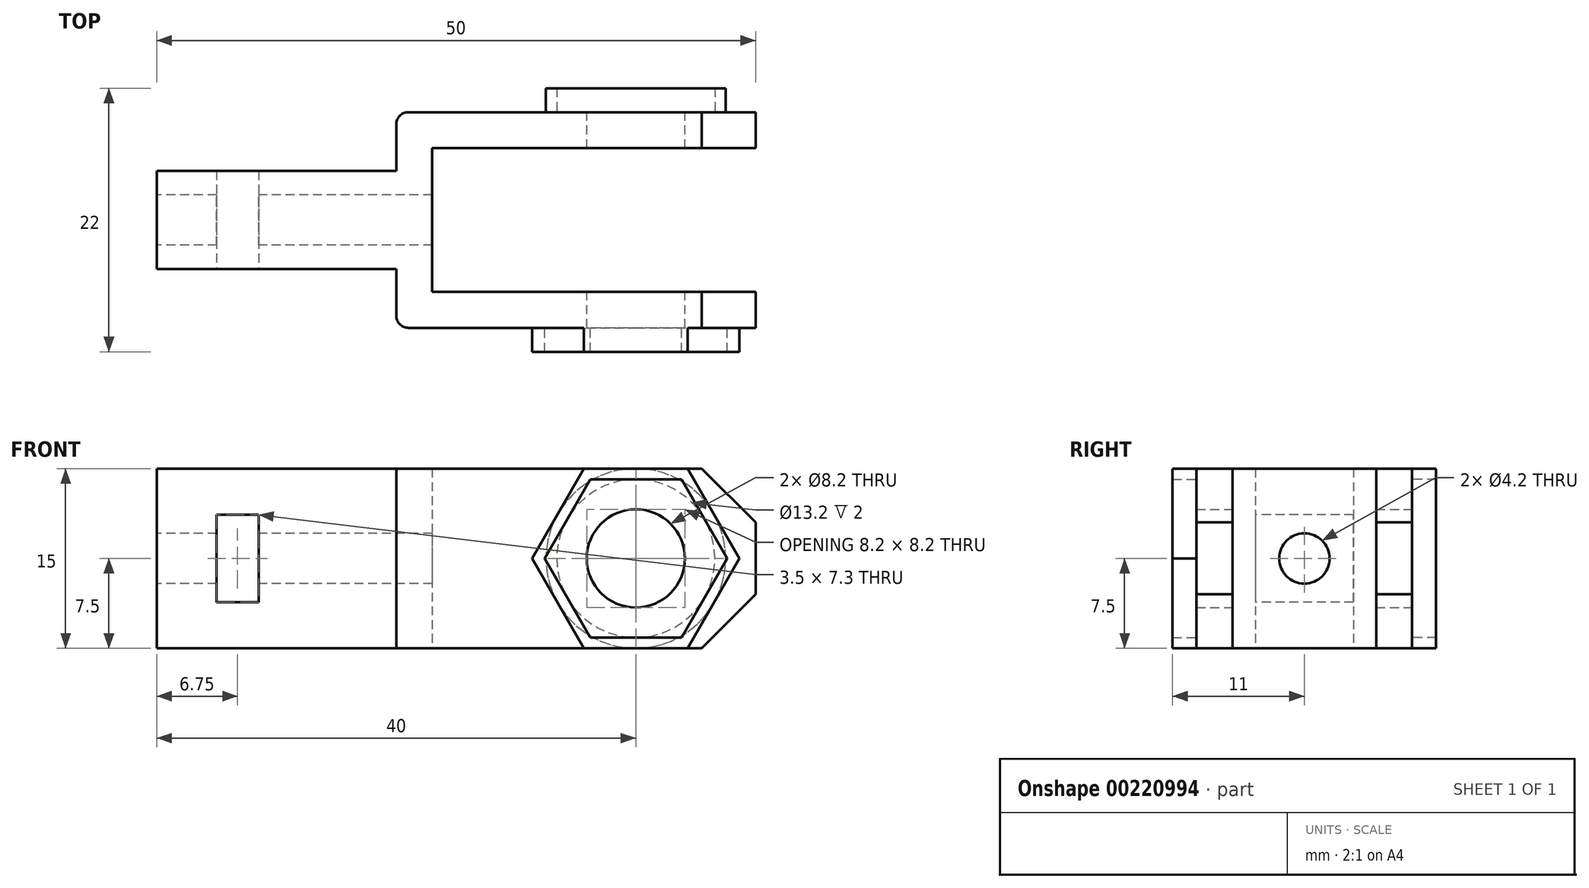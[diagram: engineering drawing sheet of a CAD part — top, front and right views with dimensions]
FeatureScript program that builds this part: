
annotation { "Feature Type Name" : "Feature", "Feature Type Description" : "" }
export const myFeature = defineFeature(function(context is Context, id is Id, definition is map)
    precondition{}
    {
        {
            var Q0;
            Q0=qCreatedBy(makeId("Top.planeOp"),FACE);
            var sketch = newSketch(context, id + "F0", { "sketchPlane" : qUnion([Q0])});
            skLineSegment(sketch, "E0", {"start": v(0, 0) * mm, "end": v(0, 4.1) * mm});
            skLineSegment(sketch, "E1", {"start": v(0, 4.1) * mm, "end": v(20, 4.1) * mm});
            skLineSegment(sketch, "E2", {"start": v(20, 4.1) * mm, "end": v(20, 8) * mm});
            skLineSegment(sketch, "E3", {"start": v(21, 9) * mm, "end": v(50, 9) * mm});
            skLineSegment(sketch, "E4", {"start": v(50, 9) * mm, "end": v(50, 6) * mm});
            skLineSegment(sketch, "E5", {"start": v(50, 6) * mm, "end": v(23, 6) * mm});
            skLineSegment(sketch, "E6", {"start": v(23, 6) * mm, "end": v(23, 0) * mm});
            skLineSegment(sketch, "E7.MirrorCS", {"start": v(50, -9) * mm, "end": v(50, -6) * mm});
            skLineSegment(sketch, "E8.MirrorCS", {"start": v(0, 0) * mm, "end": v(0, -4.1) * mm});
            skLineSegment(sketch, "E9.MirrorCS", {"start": v(23, -6) * mm, "end": v(23, 0) * mm});
            skLineSegment(sketch, "E10.MirrorCS", {"start": v(50, -6) * mm, "end": v(23, -6) * mm});
            skLineSegment(sketch, "E11.MirrorCS", {"start": v(21, -9) * mm, "end": v(50, -9) * mm});
            skLineSegment(sketch, "E12.MirrorCS", {"start": v(0, -4.1) * mm, "end": v(20, -4.1) * mm});
            skLineSegment(sketch, "E13.MirrorCS", {"start": v(20, -4.1) * mm, "end": v(20, -8) * mm});
            skPoint(sketch, "E14.visualSharp", {"position": v(20, 9) * mm});
            skArc(sketch, "E14.filletArc", {"start": v(21, 9) * mm, "mid": v(20.3, 8.7) * mm, "end": v(20, 8) * mm});
            skPoint(sketch, "E15.visualSharp", {"position": v(20, -9) * mm});
            skArc(sketch, "E15.filletArc", {"start": v(20, -8) * mm, "mid": v(20.3, -8.7) * mm, "end": v(21, -9) * mm});
            skSolve(sketch);
        }
        {
            var Q0;
            Q0 = qSketchRegion(id + "F0", true);
            extrude(context, id + "F1", {"entities" : qUnion([Q0]), "depth" : 15 * mm});
        }
        {
            var Q0;
            Q0=makeQuery(id+"F1.opExtrude","SWEPT_FACE",FACE,{"disambiguationData":[OSD([sQuery(id+"F0.wireOp",EDGE,"E0"),sQuery(id+"F0.wireOp",EDGE,"E8.MirrorCS")])]});
            var sketch = newSketch(context, id + "F2", { "sketchPlane" : qUnion([Q0])});
            skLineSegment(sketch, "E16", {"start": v(0, 0) * mm, "end": v(0, 15) * mm, "construction": true});
            skCircle(sketch, "E17", {"center": v(0, 7.5) * mm, "radius": 2.1 * mm});
            skSolve(sketch);
        }
        {
            var Q0;
            Q0 = qSketchRegion(id + "F2", true);
            extrude(context, id + "F3", {"entities" : qUnion([Q0]), "operationType" : NewBodyOperationType.REMOVE, "endBound" : BoundingType.THROUGH_ALL, "oppositeDirection" : true, "depth" : 25 * mm});
        }
        {
            var Q0;
            Q0=makeQuery(id+"F1.opExtrude","SWEPT_FACE",FACE,{"disambiguationData":[OSD([sQuery(id+"F0.wireOp",EDGE,"E12.MirrorCS")])]});
            var sketch = newSketch(context, id + "F4", { "sketchPlane" : qUnion([Q0])});
            skLineSegment(sketch, "E18", {"start": v(0, 7.5) * mm, "end": v(20, 7.5) * mm, "construction": true});
            skLineSegment(sketch, "E19.bottom", {"start": v(5, 11.15) * mm, "end": v(8.5, 11.15) * mm});
            skLineSegment(sketch, "E19.top", {"start": v(5, 3.85) * mm, "end": v(8.5, 3.85) * mm});
            skLineSegment(sketch, "E19.left", {"start": v(5, 11.15) * mm, "end": v(5, 3.85) * mm});
            skLineSegment(sketch, "E19.right", {"start": v(8.5, 11.15) * mm, "end": v(8.5, 3.85) * mm});
            skPoint(sketch, "E19.middle", {"position": v(6.75, 7.5) * mm});
            skSolve(sketch);
        }
        {
            var Q0;
            Q0 = qSketchRegion(id + "F4", true);
            extrude(context, id + "F5", {"entities" : qUnion([Q0]), "operationType" : NewBodyOperationType.REMOVE, "endBound" : BoundingType.THROUGH_ALL, "oppositeDirection" : true, "depth" : 25 * mm});
        }
        {
            var Q0;
            Q0=makeQuery(id+"F1.opExtrude","SWEPT_FACE",FACE,{"disambiguationData":[OSD([sQuery(id+"F0.wireOp",EDGE,"E3")])]});
            var sketch = newSketch(context, id + "F6", { "sketchPlane" : qUnion([Q0])});
            skLineSegment(sketch, "E20", {"start": v(-50, 7.5) * mm, "end": v(-21, 7.5) * mm, "construction": true});
            skCircle(sketch, "E21", {"center": v(-40, 7.5) * mm, "radius": 4.1 * mm});
            skLineSegment(sketch, "E22", {"start": v(-50, 15) * mm, "end": v(-45.5, 15) * mm});
            skLineSegment(sketch, "E23", {"start": v(-45.5, 15) * mm, "end": v(-50, 10.5) * mm});
            skLineSegment(sketch, "E24", {"start": v(-50, 10.5) * mm, "end": v(-50, 15) * mm});
            skLineSegment(sketch, "E25.MirrorCS", {"start": v(-50, 0) * mm, "end": v(-45.5, 0) * mm});
            skLineSegment(sketch, "E26.MirrorCS", {"start": v(-50, 4.5) * mm, "end": v(-50, 0) * mm});
            skLineSegment(sketch, "E27.MirrorCS", {"start": v(-45.5, 0) * mm, "end": v(-50, 4.5) * mm});
            skSolve(sketch);
        }
        {
            var Q0;
            Q0 = qSketchRegion(id + "F6", true);
            extrude(context, id + "F7", {"entities" : qUnion([Q0]), "operationType" : NewBodyOperationType.REMOVE, "endBound" : BoundingType.THROUGH_ALL, "oppositeDirection" : true, "depth" : 25 * mm});
        }
        {
            var Q0;
            Q0=makeQuery(id+"F1.opExtrude","SWEPT_FACE",FACE,{"disambiguationData":[OSD([sQuery(id+"F0.wireOp",EDGE,"E11.MirrorCS")])]});
            var sketch = newSketch(context, id + "F8", { "sketchPlane" : qUnion([Q0])});
            skCircle(sketch, "E28.cCircle", {"center": v(40, 7.5) * mm, "radius": 6.6 * mm, "construction": true});
            skLineSegment(sketch, "E28.0", {"start": v(36.19, 14.1) * mm, "end": v(43.81, 14.1) * mm});
            skLineSegment(sketch, "E28.1", {"start": v(43.81, 14.1) * mm, "end": v(47.62, 7.5) * mm});
            skLineSegment(sketch, "E28.2", {"start": v(47.62, 7.5) * mm, "end": v(43.81, 0.9) * mm});
            skLineSegment(sketch, "E28.3", {"start": v(43.81, 0.9) * mm, "end": v(36.19, 0.9) * mm});
            skLineSegment(sketch, "E28.4", {"start": v(36.19, 0.9) * mm, "end": v(32.38, 7.5) * mm});
            skLineSegment(sketch, "E28.5", {"start": v(32.38, 7.5) * mm, "end": v(36.19, 14.1) * mm});
            skPoint(sketch, "E28.0.midPoint", {"position": v(40, 14.1) * mm});
            skCircle(sketch, "E29.cCircle", {"center": v(40, 7.5) * mm, "radius": 7.5 * mm, "construction": true});
            skLineSegment(sketch, "E29.0", {"start": v(35.67, 15) * mm, "end": v(44.33, 15) * mm});
            skLineSegment(sketch, "E29.1", {"start": v(44.33, 15) * mm, "end": v(48.66, 7.5) * mm});
            skLineSegment(sketch, "E29.2", {"start": v(48.66, 7.5) * mm, "end": v(44.33, 0) * mm});
            skLineSegment(sketch, "E29.3", {"start": v(44.33, 0) * mm, "end": v(35.67, 0) * mm});
            skLineSegment(sketch, "E29.4", {"start": v(35.67, 0) * mm, "end": v(31.34, 7.5) * mm});
            skLineSegment(sketch, "E29.5", {"start": v(31.34, 7.5) * mm, "end": v(35.67, 15) * mm});
            skPoint(sketch, "E29.0.midPoint", {"position": v(40, 15) * mm});
            skSolve(sketch);
        }
        {
            var Q0;
            Q0 = qSketchRegion(id + "F8", true);
            extrude(context, id + "F9", {"entities" : qUnion([Q0]), "operationType" : NewBodyOperationType.ADD, "depth" : 2 * mm});
        }
        {
            var Q0;
            Q0=makeQuery(id+"F1.opExtrude","SWEPT_FACE",FACE,{"disambiguationData":[OSD([sQuery(id+"F0.wireOp",EDGE,"E3")])]});
            var sketch = newSketch(context, id + "F10", { "sketchPlane" : qUnion([Q0])});
            skCircle(sketch, "E30", {"center": v(-40, 7.5) * mm, "radius": 6.6 * mm});
            skCircle(sketch, "E31", {"center": v(-40, 7.5) * mm, "radius": 7.5 * mm});
            skSolve(sketch);
        }
        {
            var Q0;
            Q0 = qSketchRegion(id + "F10", true);
            extrude(context, id + "F11", {"entities" : qUnion([Q0]), "operationType" : NewBodyOperationType.ADD, "depth" : 2 * mm});
        }
    });
